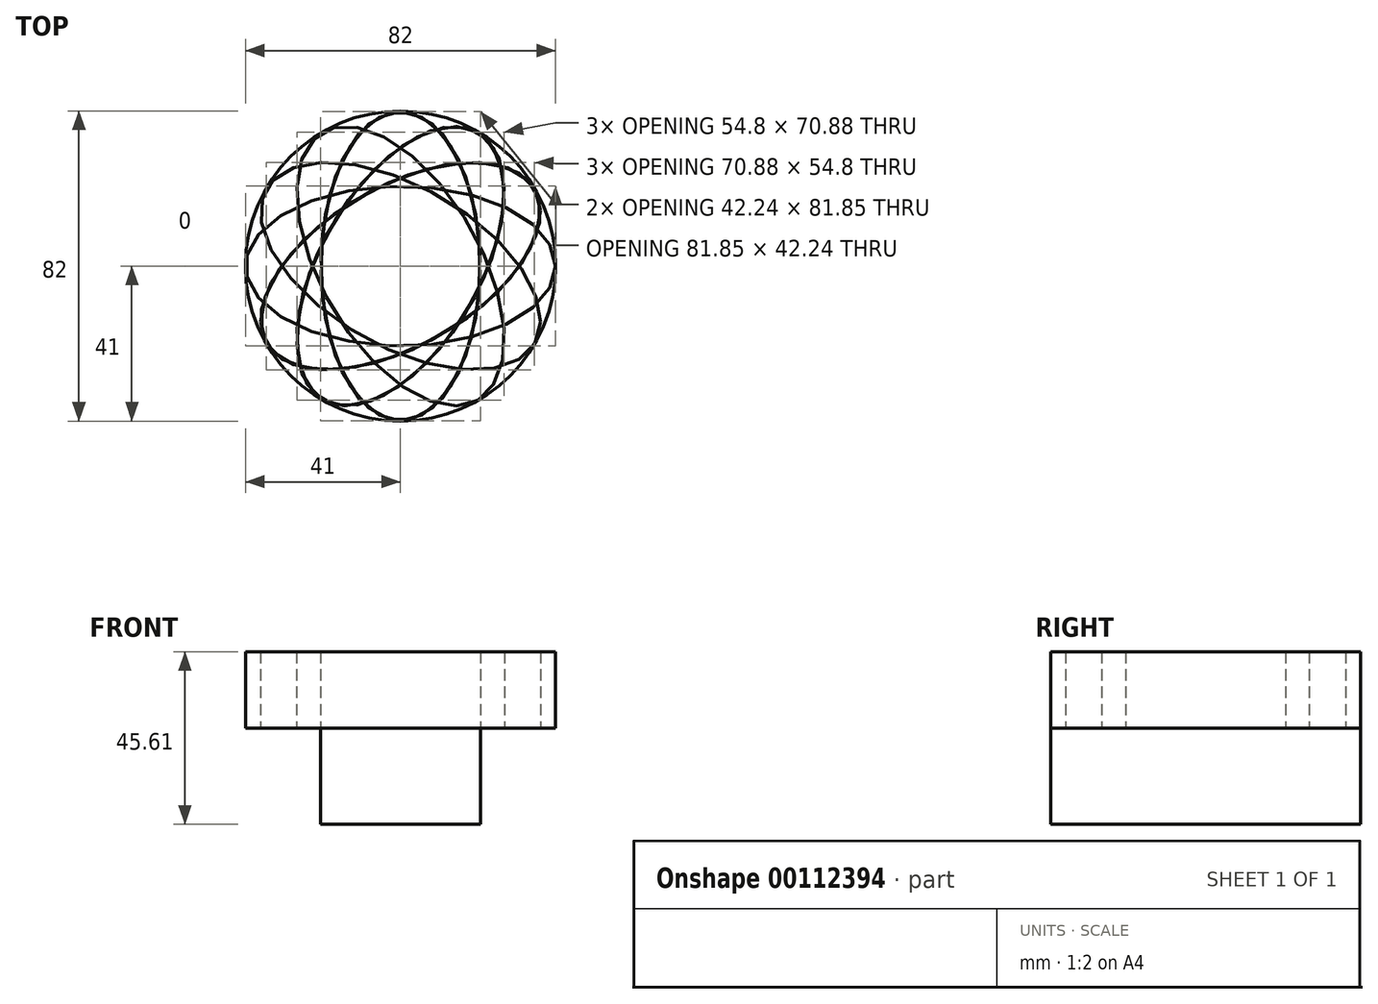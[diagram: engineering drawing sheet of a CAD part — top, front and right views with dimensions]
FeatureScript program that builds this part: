
annotation { "Feature Type Name" : "Feature", "Feature Type Description" : "" }
export const myFeature = defineFeature(function(context is Context, id is Id, definition is map)
    precondition{}
    {
        {
            var Q0;
            Q0=qCreatedBy(makeId("Top.planeOp"),FACE);
            var sketch = newSketch(context, id + "F0", { "sketchPlane" : qUnion([Q0])});
            skEllipse(sketch, "E0", {"center": v(33.21, 0) * mm, "majorRadius": 40.92 * mm, "minorRadius": 21.12 * mm, "majorAxis": v(0, 1)});
            skSolve(sketch);
        }
        {
            var Q0;
            Q0=makeQuery(id+"F0.imprint","IMPRINT",FACE,{"disambiguationData":[TD([[makeQuery(id+"F0.imprint","IMPRINT",EDGE,{"derivedFrom":sQuery(id+"F0.wireOp",EDGE,"E0")}),1.0]])]});
            extrude(context, id + "F1", {"entities" : qUnion([Q0]), "depth" : 25.4 * mm});
        }
        {
            var Q0;
            Q0=makeQuery(id+"F1.opExtrude","CAP_FACE",FACE,{"disambiguationData":[OSD([sQuery(id+"F0.wireOp",EDGE,"E0")])],"isStart":false});
            var sketch = newSketch(context, id + "F2", { "sketchPlane" : qUnion([Q0])});
            skCircle(sketch, "E1", {"center": v(33.21, 0) * mm, "radius": 41 * mm});
            skSolve(sketch);
        }
        {
            var Q0;
            Q0=makeQuery(id+"F2.imprint","IMPRINT",FACE,{"disambiguationData":[TD([[makeQuery(id+"F2.imprint","IMPRINT",EDGE,{"derivedFrom":sQuery(id+"F2.wireOp",EDGE,"E1")}),1.0]])]});
            var sketch = newSketch(context, id + "F3", { "sketchPlane" : qUnion([Q0])});
            skSolve(sketch);
        }
        {
            var Q0;
            Q0 = qSketchRegion(id + "F3", true);
            var Q1;
            Q1=makeQuery(id+"F2.imprint","IMPRINT",FACE,{"disambiguationData":[TD([[makeQuery(id+"F2.imprint","IMPRINT",EDGE,{"derivedFrom":sQuery(id+"F2.wireOp",EDGE,"E1")}),1.0]])]});
            extrude(context, id + "F4", {"entities" : qUnion([Q0, Q1]), "depth" : 20.2 * mm});
        }
        {
            var Q0;
            Q0=makeQuery(id+"F4.opExtrude","SWEPT_BODY",BODY,{"disambiguationData":[OSD([sQuery(id+"F0.wireOp",EDGE,"E0"),sQuery(id+"F2.wireOp",EDGE,"E1")])]});
            var Q1;
            Q1=makeQuery(id+"F4.opExtrude","CAP_EDGE",EDGE,{"disambiguationData":[OSD([sQuery(id+"F2.wireOp",EDGE,"E1")])],"isStart":false});
            circularPattern(context, id + "F5", {"entities" : qUnion([Q0]), "axis" : qUnion([Q1]), "angle" : 30 * degree, "instanceCount" : 9, "oppositeDirection" : true});
        }
    });
